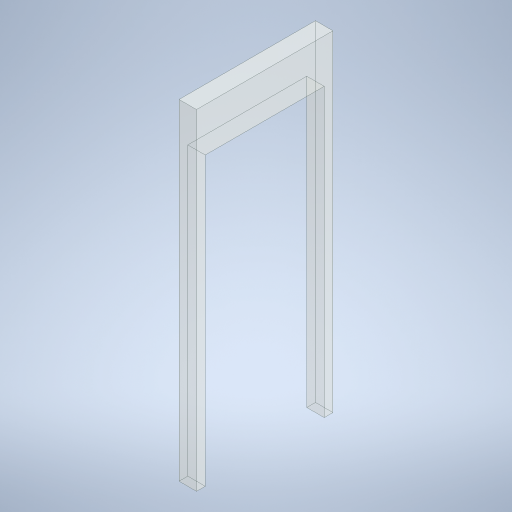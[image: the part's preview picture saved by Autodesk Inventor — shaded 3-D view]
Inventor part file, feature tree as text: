
AUTODESK INVENTOR PART (.ipt)
format: ipt  version: 2024 (Build 280153000, 153)  size: 252,928 bytes
history: native  units: in
note: dims shown in document units (in); Inventor stores cm internally (conversion verified against a paired STEP export)
features: extrude x2, sketch x2
ambient origin geometry x8: Origin, YZ Plane, XZ Plane, XY Plane, X Axis, Y Axis, Z Axis, Center Point
bodies: Solid1 (feature_tree)
feature tree (4):
  extrude  "Extrusion1"  Depth=94.5in
  extrude  "Extrusion2"  Depth=82.0in
  sketch  "Sketch1"  dims[d0=39.0in d1=94.5in]
  sketch  "Sketch2"  dims[d2=5.0in d3=0.0in d4=82.0in d6=2.5in d7=34.0in d8=1.0in d9=0.0in]
